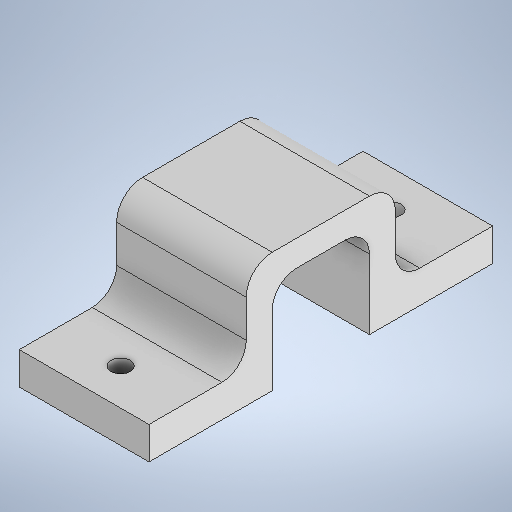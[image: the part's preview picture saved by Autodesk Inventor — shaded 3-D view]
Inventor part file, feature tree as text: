
AUTODESK INVENTOR PART (.ipt)
format: ipt  version: 2025.1 (Build 291241020, 241B)  size: 260,608 bytes
history: native  units: in
note: dims shown in document units (in); Inventor stores cm internally (conversion verified against a paired STEP export)
features: fillet x5, extrude x3, sketch x3
ambient origin geometry x8: Origin, YZ Plane, XZ Plane, XY Plane, X Axis, Y Axis, Z Axis, Center Point
bodies: Solid1 (feature_tree)
feature tree (11):
  extrude  "Extrusion1"  Depth=0.75in
  fillet  "Fillet1"  Radius=0.725in
  fillet  "Fillet2"  Radius=0.2in
  fillet  "Fillet3"  Radius=0.2in
  fillet  "Fillet4"  Radius=0.2in
  fillet  "Fillet5"  Radius=0.25in
  extrude  "Extrusion2"  Depth=0.95in
  extrude  "Extrusion3"  Depth=1.0in TaperAngle=0.0deg
  sketch  "Sketch1"  dims[d2=0.725in d3=0.75in d4=0.725in d5=0.2in d6=0.2in d7=0.2in d8=0.25in]
  sketch  "Sketch3"  dims[d9=0.25in d10=0.95in]
  sketch  "Sketch4"  dims[d11=0.95in d12=1.0in d13=0.0in d26=0.1875in d27=0.1875in d28=0.1875in d29=0.1875in d30=0.2in d31=0.15in d32=0.5in d33=0.2815in d34=1.0in d35=0.0in d36=0.15in d37=0.5in d38=0.2815in d39=1.0in d40=0.0in]
